# Revit family: R-MTD-306
name_source: partatom
category: Portes
units: mm (PartAtom-declared; Revit-internal decimal feet)

## family parameters
Couper avec des vides une fois chargée = Non
Hôte = Mur
Partagée = Non
Repère de localisation dans la pièce = Non
Toujours verticalement = Oui

## types (2) — shared parameters
1 Vantail = Oui
2 Vantaux = Non
Construction analytique = <Aucun>
DC Fixation_Rail = 150 mm  [stored 0.492126 ft]
Ep Butée = 178 mm  [stored 0.58399 ft]
Ep Chicane Murale = 200 mm  [stored 0.656168 ft]
Ep Face Coté Opposé Baie = 10 mm  [stored 0.0328084 ft]
Ep Fond Butée = 11 mm  [stored 0.0360892 ft]
Ep Rail = 3 mm  [stored 0.00984252 ft]
Fabricant = MALERBA
Grille Vantail Principal = Non
Grille Vantail Secondaire = Non
Grille toute hauteur = Non
Hauteur Profil Rail = 44 mm
Hauteur chandelle support grille = 180 mm  [stored 0.590551 ft]
Hauteur sous Dalle = 2500 mm  [stored 8.2021 ft]
Ht Fixation Linteau = 430 mm
Jeu Portillon Bas = 51 mm
Jeu Portillon Coté Opposé Pivot = 10 mm  [stored 0.0328084 ft]
Jeu Portillon Coté Pivot = 10 mm  [stored 0.0328084 ft]
Jeu Portillon Haut = 10 mm  [stored 0.0328084 ft]
Jeu Vantail Bas = 10 mm  [stored 0.0328084 ft]
Larg Portillon = 900 mm  [stored 2.95276 ft]
Larg Vantail Primaire Asymétrique = 2400 mm
Mat Ame = Prépeint
Mat Grille = Grille
Mat Quinc = Acier galvanisé
Mat Support = Peinture Laquée PMT - Gris Anthracite - RAL 7016
Materiaux_Dominant = Métal
Montage sur Mur Perpendiculaire = Non
Position Vantail Mur = 91 mm  [stored 0.298556 ft]
Prof Butée = 260 mm  [stored 0.853018 ft]
Profondeur Rail = 49 mm  [stored 0.160761 ft]
Rec Arrière = 215 mm
Rec Avant = 160 mm  [stored 0.524934 ft]
Rec Haut = 200 mm  [stored 0.656168 ft]
Retours Rails = 17 mm
URL = https://www.malerba.fr
Vantaux Asymétriques = Non
zero-valued in all types: DC Jeu Avant, DC Jeu Haut, DC Portillon, DC Profil Butée, Désax 2V Asymétrique, Thermique (W/m2.°K)

## per-type parameters (varying)
- MTD-306: Angle Rail 1=2.00°; Angle Rail 2=2.00°; Butée en L=Non; Butée en U=Oui; Certification=D.A.S. Mode 2 certifié NF; Code_MAJ=2301110401MTD306; DAS=Oui; Description=Bloc-porte métal industriel D.A.S. M 1201 S - DAS système coulissant avec des modules coulissants de 1 panneau en hauteur, EI120, D.A.S. certifié NF, sur rail incliné ou droit, avec guidage au sol; Ep Face Coté Baie=5 mm  [stored 0.0164042 ft]; Ep Vantail=100 mm  [stored 0.328084 ft]; Fiche_Produit=MTD-306; Fixation Linteau=Oui; Fixation sous Dalle=Non; Hauteur Baie=2500 mm  [stored 8.2021 ft]; Ht Portillon=2300 mm; Largeur Baie=3000 mm  [stored 9.84252 ft]; Lgt Fix Vantail Primaire=6325 mm  [stored 20.7513 ft]; Lgt Fix Vantail Second=6325 mm  [stored 20.7513 ft]; Lgt Rail Second=6825 mm  [stored 22.3917 ft]; Note d'identification=1V EI120 - DAS COULISSANT - 1 PANNEAU; Prof Chicane Murale=30 mm  [stored 0.0984252 ft]; Prof Coté Butée=30 mm  [stored 0.0984252 ft]; Reference_Commerciale=M 1201 S - DAS; Resistance_Feu=EI120; Sens_Feu=Recto / Verso; lgt Rail Primaire=6825 mm  [stored 22.3917 ft]
- 17 - Coulissante 2: Angle Rail 1=1.00°; Angle Rail 2=1.00°; Butée en L=Oui; Butée en U=Non; DAS=Non; Ep Face Coté Baie=10 mm  [stored 0.0328084 ft]; Ep Vantail=82 mm  [stored 0.269029 ft]; Fixation Linteau=Non; Fixation sous Dalle=Oui; Hauteur Baie=2300 mm; Ht Portillon=2000 mm  [stored 6.56168 ft]; Largeur Baie=5000 mm  [stored 16.4042 ft]; Lgt Fix Vantail Primaire=10325 mm; Lgt Fix Vantail Second=10325 mm; Lgt Rail Second=10825 mm; Prof Chicane Murale=50 mm  [stored 0.164042 ft]; Prof Coté Butée=71 mm; lgt Rail Primaire=10825 mm

note: [stored X ft] marks values corroborated as IEEE doubles in the binary element streams (Revit-internal decimal feet)

## geometry (parser evidence)
native form markers: Blend x12
no freeform markers — native parametric forms only
